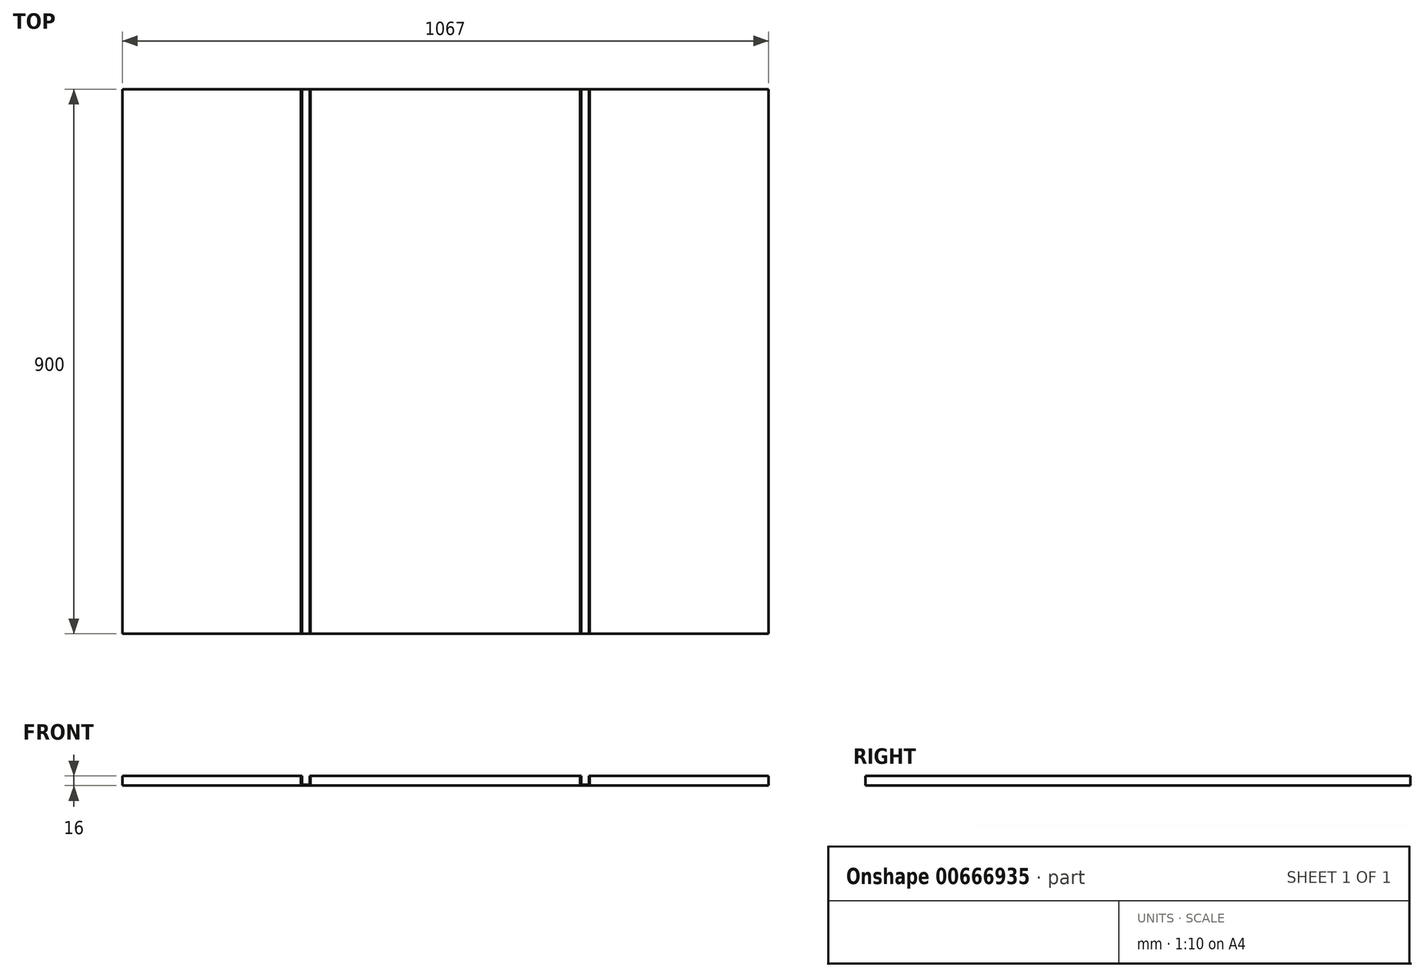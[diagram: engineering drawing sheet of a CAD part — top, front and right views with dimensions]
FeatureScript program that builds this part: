
annotation { "Feature Type Name" : "Feature", "Feature Type Description" : "" }
export const myFeature = defineFeature(function(context is Context, id is Id, definition is map)
    precondition{}
    {
        {
            var Q0;
            Q0=qCreatedBy(makeId("Top.planeOp"),FACE);
            var sketch = newSketch(context, id + "F0", { "sketchPlane" : qUnion([Q0])});
            skLineSegment(sketch, "E0.bottom", {"start": v(-533.5, 450) * mm, "end": v(-238.5, 450) * mm});
            skLineSegment(sketch, "E0.top", {"start": v(-533.5, -450) * mm, "end": v(-238.5, -450) * mm});
            skLineSegment(sketch, "E0.left", {"start": v(-533.5, 450) * mm, "end": v(-533.5, -450) * mm});
            skLineSegment(sketch, "E0.right", {"start": v(533.5, 450) * mm, "end": v(533.5, -450) * mm});
            skPoint(sketch, "E0.middle", {"position": v(0, 0) * mm});
            skLineSegment(sketch, "E1", {"start": v(-222.5, 450) * mm, "end": v(-222.5, -450) * mm});
            skLineSegment(sketch, "E2", {"start": v(222.5, 450) * mm, "end": v(222.5, -450) * mm});
            skLineSegment(sketch, "E3", {"start": v(-238.5, 450) * mm, "end": v(-238.5, -450) * mm});
            skLineSegment(sketch, "E4", {"start": v(238.5, 450) * mm, "end": v(238.5, -450) * mm});
            skLineSegment(sketch, "E5", {"start": v(0, 450) * mm, "end": v(0, -450) * mm, "construction": true});
            skLineSegment(sketch, "E6", {"start": v(-222.5, 0) * mm, "end": v(222.5, 0) * mm, "construction": true});
            skLineSegment(sketch, "E7", {"start": v(-238.5, 450) * mm, "end": v(-222.5, 450) * mm});
            skLineSegment(sketch, "E8", {"start": v(-222.5, 450) * mm, "end": v(222.5, 450) * mm});
            skLineSegment(sketch, "E9", {"start": v(222.5, 450) * mm, "end": v(238.5, 450) * mm});
            skLineSegment(sketch, "E10", {"start": v(238.5, 450) * mm, "end": v(533.5, 450) * mm});
            skLineSegment(sketch, "E11", {"start": v(-238.5, -450) * mm, "end": v(-222.5, -450) * mm});
            skLineSegment(sketch, "E12", {"start": v(-222.5, -450) * mm, "end": v(222.5, -450) * mm});
            skLineSegment(sketch, "E13", {"start": v(222.5, -450) * mm, "end": v(238.5, -450) * mm});
            skLineSegment(sketch, "E14", {"start": v(238.5, -450) * mm, "end": v(533.5, -450) * mm});
            skLineSegment(sketch, "E15", {"start": v(-230.5, 450) * mm, "end": v(-230.5, -450) * mm});
            skLineSegment(sketch, "E16", {"start": v(230.5, -450) * mm, "end": v(230.5, 450) * mm});
            skSolve(sketch);
        }
        {
            var Q0;
            {var subQ0=sQuery(id+"F0.wireOp",EDGE,"E0.left");Q0=makeQuery(id+"F0.imprint","IMPRINT",FACE,{"disambiguationData":[TD([[makeQuery(id+"F0.imprint","IMPRINT",EDGE,{"derivedFrom":subQ0}),1.0]])]});}
            var Q1;
            {var subQ0=sQuery(id+"F0.wireOp",EDGE,"E1");Q1=makeQuery(id+"F0.imprint","IMPRINT",FACE,{"disambiguationData":[TD([[makeQuery(id+"F0.imprint","IMPRINT",EDGE,{"derivedFrom":subQ0}),1.0]])]});}
            var Q2;
            {var subQ0=sQuery(id+"F0.wireOp",EDGE,"E0.right");Q2=makeQuery(id+"F0.imprint","IMPRINT",FACE,{"disambiguationData":[TD([[makeQuery(id+"F0.imprint","IMPRINT",EDGE,{"derivedFrom":subQ0}),-1.0]])]});}
            extrude(context, id + "F1", {"entities" : qUnion([Q0, Q1, Q2]), "depth" : 16 * mm, "offsetDistance" : 25 * mm});
        }
        {
            var Q0;
            Q0=qCreatedBy(makeId("Front.planeOp"),FACE);
            var sketch = newSketch(context, id + "F2", { "sketchPlane" : qUnion([Q0])});
            skLineSegment(sketch, "E17", {"start": v(-238.5, 16) * mm, "end": v(-238.5, 0) * mm});
            skLineSegment(sketch, "E18", {"start": v(-238.5, 0) * mm, "end": v(-222.5, 0) * mm});
            skLineSegment(sketch, "E19", {"start": v(-222.5, 0) * mm, "end": v(-222.5, 16) * mm});
            skLineSegment(sketch, "E20.0", {"start": v(-224, 1.5) * mm, "end": v(-224, 16) * mm});
            skLineSegment(sketch, "E20.1", {"start": v(-237, 1.5) * mm, "end": v(-224, 1.5) * mm});
            skLineSegment(sketch, "E20.2", {"start": v(-237, 16) * mm, "end": v(-237, 1.5) * mm});
            skLineSegment(sketch, "E21", {"start": v(-238.5, 16) * mm, "end": v(-237, 16) * mm});
            skLineSegment(sketch, "E22", {"start": v(-224, 16) * mm, "end": v(-222.5, 16) * mm});
            skLineSegment(sketch, "E23", {"start": v(0, 0) * mm, "end": v(0, 16) * mm, "construction": true});
            skLineSegment(sketch, "E24.MirrorCS", {"start": v(238.5, 16) * mm, "end": v(237, 16) * mm});
            skLineSegment(sketch, "E25.MirrorCS", {"start": v(237, 1.5) * mm, "end": v(224, 1.5) * mm});
            skLineSegment(sketch, "E26.MirrorCS", {"start": v(224, 16) * mm, "end": v(222.5, 16) * mm});
            skLineSegment(sketch, "E27.MirrorCS", {"start": v(238.5, 0) * mm, "end": v(222.5, 0) * mm});
            skLineSegment(sketch, "E28.MirrorCS", {"start": v(237, 16) * mm, "end": v(237, 1.5) * mm});
            skLineSegment(sketch, "E29.MirrorCS", {"start": v(238.5, 16) * mm, "end": v(238.5, 0) * mm});
            skLineSegment(sketch, "E30.MirrorCS", {"start": v(222.5, 0) * mm, "end": v(222.5, 16) * mm});
            skLineSegment(sketch, "E31.MirrorCS", {"start": v(224, 1.5) * mm, "end": v(224, 16) * mm});
            skSolve(sketch);
        }
        {
            var Q0;
            Q0 = qSketchRegion(id + "F2", true);
            extrude(context, id + "F3", {"entities" : qUnion([Q0]), "endBound" : BoundingType.SYMMETRIC, "depth" : 900 * mm, "offsetDistance" : 25 * mm});
        }
    });
